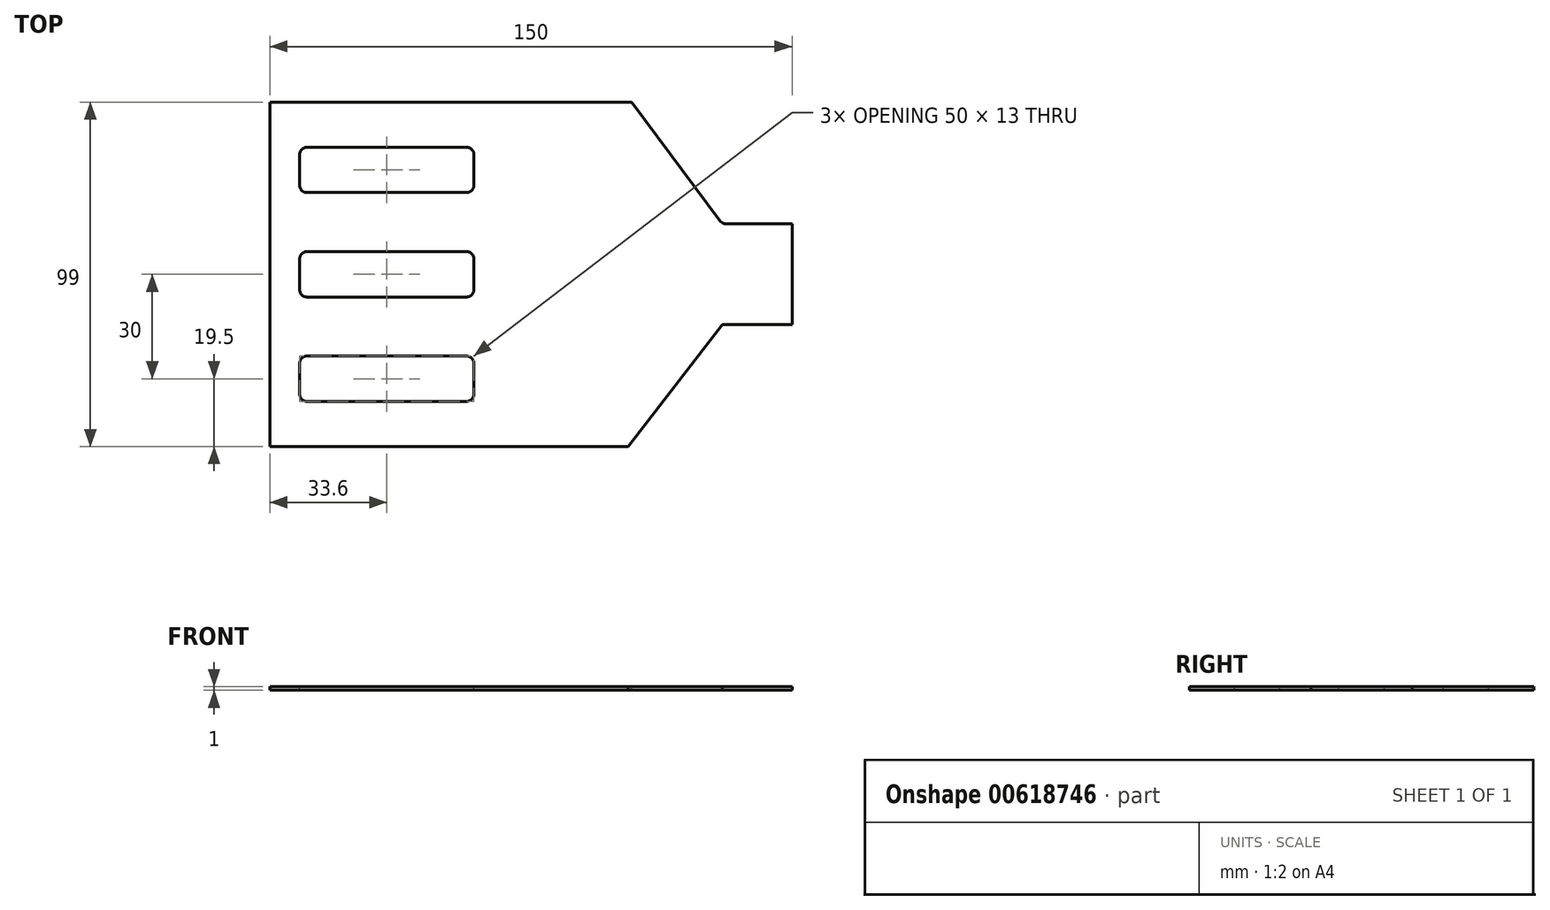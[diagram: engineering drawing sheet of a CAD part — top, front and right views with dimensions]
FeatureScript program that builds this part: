
annotation { "Feature Type Name" : "Feature", "Feature Type Description" : "" }
export const myFeature = defineFeature(function(context is Context, id is Id, definition is map)
    precondition{}
    {
        {
            var Q0;
            Q0=qCreatedBy(makeId("Top.planeOp"),FACE);
            var sketch = newSketch(context, id + "F0", { "sketchPlane" : qUnion([Q0])});
            skPoint(sketch, "E0", {"position": v(0, 0) * mm});
            skLineSegment(sketch, "E1.bottom", {"start": v(75, 49.5) * mm, "end": v(-75, 49.5) * mm});
            skLineSegment(sketch, "E1.top", {"start": v(75, -49.5) * mm, "end": v(-75, -49.5) * mm});
            skLineSegment(sketch, "E1.left", {"start": v(75, 49.5) * mm, "end": v(75, -49.5) * mm});
            skLineSegment(sketch, "E1.right", {"start": v(-75, 49.5) * mm, "end": v(-75, -49.5) * mm});
            skSolve(sketch);
        }
        {
            var Q0;
            Q0 = qSketchRegion(id + "F0", true);
            extrude(context, id + "F1", {"entities" : qUnion([Q0]), "depth" : 1 * mm, "offsetDistance" : 25 * mm});
        }
        {
            var Q0;
            Q0=makeQuery(id+"F1.opExtrude","CAP_FACE",FACE,{"disambiguationData":[OSD([sQuery(id+"F0.wireOp",EDGE,"E1.bottom"),sQuery(id+"F0.wireOp",EDGE,"E1.top"),sQuery(id+"F0.wireOp",EDGE,"E1.left"),sQuery(id+"F0.wireOp",EDGE,"E1.right")])],"isStart":false});
            var sketch = newSketch(context, id + "F2", { "sketchPlane" : qUnion([Q0])});
            skLineSegment(sketch, "E2", {"start": v(-66.4, 34.5) * mm, "end": v(-66.4, 25.5) * mm});
            skLineSegment(sketch, "E3", {"start": v(-64.4, 23.5) * mm, "end": v(-18.4, 23.5) * mm});
            skLineSegment(sketch, "E4", {"start": v(-16.4, 25.5) * mm, "end": v(-16.4, 34.5) * mm});
            skLineSegment(sketch, "E5", {"start": v(-18.4, 36.5) * mm, "end": v(-64.4, 36.5) * mm});
            skLineSegment(sketch, "E6", {"start": v(-66.4, 4.5) * mm, "end": v(-66.4, -4.5) * mm});
            skLineSegment(sketch, "E7", {"start": v(-64.4, -6.5) * mm, "end": v(-18.4, -6.5) * mm});
            skLineSegment(sketch, "E8", {"start": v(-16.4, -4.5) * mm, "end": v(-16.4, 4.5) * mm});
            skLineSegment(sketch, "E9", {"start": v(-18.4, 6.5) * mm, "end": v(-64.4, 6.5) * mm});
            skLineSegment(sketch, "E10", {"start": v(-66.4, -25.5) * mm, "end": v(-66.4, -34.5) * mm});
            skLineSegment(sketch, "E11", {"start": v(-64.4, -36.5) * mm, "end": v(-18.4, -36.5) * mm});
            skLineSegment(sketch, "E12", {"start": v(-16.4, -34.5) * mm, "end": v(-16.4, -25.5) * mm});
            skLineSegment(sketch, "E13", {"start": v(-18.4, -23.5) * mm, "end": v(-64.4, -23.5) * mm});
            skLineSegment(sketch, "E14", {"start": v(75, 14.5) * mm, "end": v(56, 14.5) * mm});
            skLineSegment(sketch, "E15", {"start": v(54.4, 15.3) * mm, "end": v(28.95, 49.5) * mm});
            skLineSegment(sketch, "E16", {"start": v(75, -14.5) * mm, "end": v(55, -14.5) * mm});
            skLineSegment(sketch, "E17", {"start": v(55, -14.5) * mm, "end": v(27.87, -49.5) * mm});
            skPoint(sketch, "E18.visualSharp", {"position": v(-66.4, 36.5) * mm});
            skArc(sketch, "E18.filletArc", {"start": v(-64.4, 36.5) * mm, "mid": v(-65.81, 35.91) * mm, "end": v(-66.4, 34.5) * mm});
            skPoint(sketch, "E19.visualSharp", {"position": v(-16.4, 36.5) * mm});
            skArc(sketch, "E19.filletArc", {"start": v(-16.4, 34.5) * mm, "mid": v(-16.99, 35.91) * mm, "end": v(-18.4, 36.5) * mm});
            skPoint(sketch, "E20.visualSharp", {"position": v(-16.4, 23.5) * mm});
            skArc(sketch, "E20.filletArc", {"start": v(-18.4, 23.5) * mm, "mid": v(-16.99, 24.09) * mm, "end": v(-16.4, 25.5) * mm});
            skPoint(sketch, "E21.visualSharp", {"position": v(-66.4, 23.5) * mm});
            skArc(sketch, "E21.filletArc", {"start": v(-66.4, 25.5) * mm, "mid": v(-65.81, 24.09) * mm, "end": v(-64.4, 23.5) * mm});
            skPoint(sketch, "E22.visualSharp", {"position": v(-66.4, 6.5) * mm});
            skArc(sketch, "E22.filletArc", {"start": v(-64.4, 6.5) * mm, "mid": v(-65.81, 5.91) * mm, "end": v(-66.4, 4.5) * mm});
            skPoint(sketch, "E23.visualSharp", {"position": v(-66.4, -6.5) * mm});
            skArc(sketch, "E23.filletArc", {"start": v(-66.4, -4.5) * mm, "mid": v(-65.81, -5.91) * mm, "end": v(-64.4, -6.5) * mm});
            skPoint(sketch, "E24.visualSharp", {"position": v(-16.4, -6.5) * mm});
            skArc(sketch, "E24.filletArc", {"start": v(-18.4, -6.5) * mm, "mid": v(-16.99, -5.91) * mm, "end": v(-16.4, -4.5) * mm});
            skPoint(sketch, "E25.visualSharp", {"position": v(-16.4, 6.5) * mm});
            skArc(sketch, "E25.filletArc", {"start": v(-16.4, 4.5) * mm, "mid": v(-16.99, 5.91) * mm, "end": v(-18.4, 6.5) * mm});
            skPoint(sketch, "E26.visualSharp", {"position": v(-16.4, -23.5) * mm});
            skArc(sketch, "E26.filletArc", {"start": v(-16.4, -25.5) * mm, "mid": v(-16.99, -24.09) * mm, "end": v(-18.4, -23.5) * mm});
            skPoint(sketch, "E27.visualSharp", {"position": v(-16.4, -36.5) * mm});
            skArc(sketch, "E27.filletArc", {"start": v(-18.4, -36.5) * mm, "mid": v(-16.99, -35.91) * mm, "end": v(-16.4, -34.5) * mm});
            skPoint(sketch, "E28.visualSharp", {"position": v(-66.4, -36.5) * mm});
            skArc(sketch, "E28.filletArc", {"start": v(-66.4, -34.5) * mm, "mid": v(-65.81, -35.91) * mm, "end": v(-64.4, -36.5) * mm});
            skPoint(sketch, "E29.visualSharp", {"position": v(-66.4, -23.5) * mm});
            skArc(sketch, "E29.filletArc", {"start": v(-64.4, -23.5) * mm, "mid": v(-65.81, -24.09) * mm, "end": v(-66.4, -25.5) * mm});
            skPoint(sketch, "E30.visualSharp", {"position": v(55, 14.5) * mm});
            skArc(sketch, "E30.filletArc", {"start": v(54.4, 15.3) * mm, "mid": v(55.1, 14.71) * mm, "end": v(56, 14.5) * mm});
            skSolve(sketch);
        }
        {
            var Q0;
            Q0 = qSketchRegion(id + "F2", true);
            var Q1;
            {var subQ0=sQuery(id+"F2.wireOp",EDGE,"E14");Q1=makeQuery(id+"F2.imprint","IMPRINT",FACE,{"disambiguationData":[TD([[makeQuery(id+"F2.imprint","IMPRINT",EDGE,{"derivedFrom":subQ0}),-1.0]])]});}
            var Q2;
            {var subQ0=sQuery(id+"F2.wireOp",EDGE,"E16");Q2=makeQuery(id+"F2.imprint","IMPRINT",FACE,{"disambiguationData":[TD([[makeQuery(id+"F2.imprint","IMPRINT",EDGE,{"derivedFrom":subQ0}),1.0]])]});}
            extrude(context, id + "F3", {"entities" : qUnion([Q0, Q1, Q2]), "operationType" : NewBodyOperationType.REMOVE, "oppositeDirection" : true, "depth" : 25 * mm, "offsetDistance" : 25 * mm});
        }
    });
